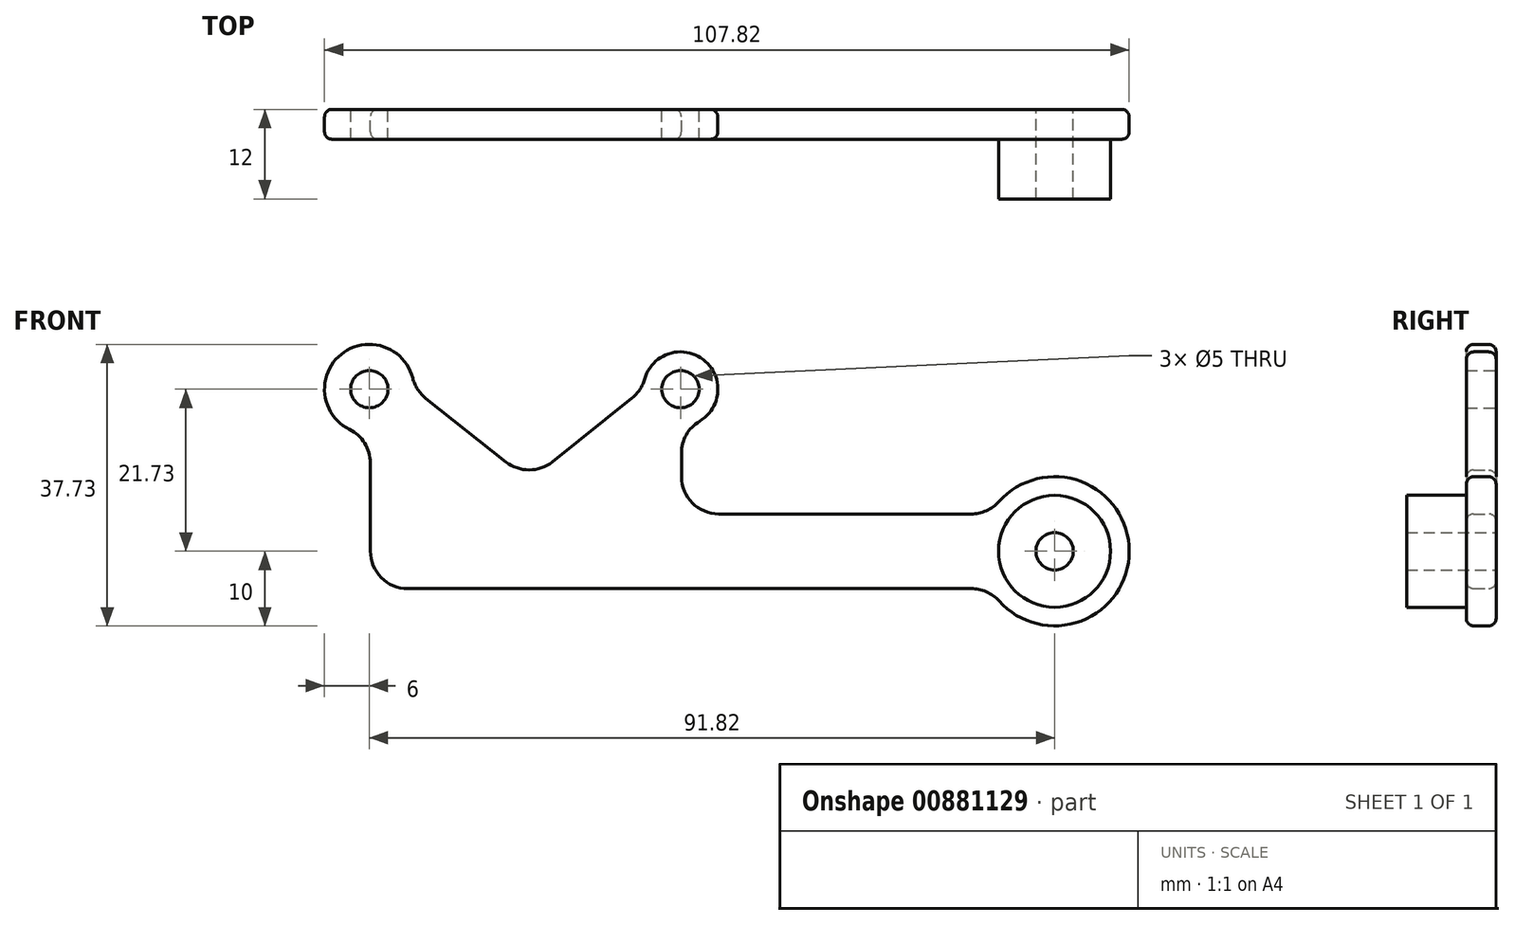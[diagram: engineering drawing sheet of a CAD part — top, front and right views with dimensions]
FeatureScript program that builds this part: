
annotation { "Feature Type Name" : "Feature", "Feature Type Description" : "" }
export const myFeature = defineFeature(function(context is Context, id is Id, definition is map)
    precondition{}
    {
        {
            var Q0;
            Q0=qCreatedBy(makeId("Front.planeOp"),FACE);
            var sketch = newSketch(context, id + "F0", { "sketchPlane" : qUnion([Q0])});
            skCircle(sketch, "E0", {"center": v(0, 0) * mm, "radius": 2.5 * mm});
            skCircle(sketch, "E1", {"center": v(41.7, 0) * mm, "radius": 2.5 * mm});
            skArc(sketch, "E2", {"start": v(5.82, 1.46) * mm, "mid": v(-3.77, 4.67) * mm, "end": v(-2.65, -5.38) * mm});
            skArc(sketch, "E3", {"start": v(44.26, -4.3) * mm, "mid": v(44.74, 3.97) * mm, "end": v(36.89, 1.35) * mm});
            skLineSegment(sketch, "E4", {"start": v(0.14, -9.87) * mm, "end": v(0.14, -21.73) * mm});
            skPoint(sketch, "E5.visualSharp", {"position": v(0.14, -6) * mm});
            skArc(sketch, "E5.filletArc", {"start": v(0.14, -9.87) * mm, "mid": v(-0.61, -7.23) * mm, "end": v(-2.65, -5.38) * mm});
            skPoint(sketch, "E6.visualSharp", {"position": v(41.82, -5) * mm});
            skArc(sketch, "E6.filletArc", {"start": v(44.26, -4.3) * mm, "mid": v(42.47, -6.12) * mm, "end": v(41.82, -8.59) * mm});
            skPoint(sketch, "E7.visualSharp", {"position": v(6, 0) * mm});
            skPoint(sketch, "E8.visualSharp", {"position": v(36.7, 0) * mm});
            skCircle(sketch, "E9", {"center": v(91.82, -21.73) * mm, "radius": 2.5 * mm});
            skArc(sketch, "E10", {"start": v(84.37, -28.4) * mm, "mid": v(101.82, -21.73) * mm, "end": v(84.37, -15.06) * mm});
            skLineSegment(sketch, "E11.0", {"start": v(5.14, -26.73) * mm, "end": v(80.64, -26.73) * mm});
            skLineSegment(sketch, "E12.0", {"start": v(46.82, -16.73) * mm, "end": v(80.64, -16.73) * mm});
            skLineSegment(sketch, "E13.trimOffspring", {"start": v(41.82, -11.73) * mm, "end": v(41.82, -8.59) * mm});
            skPoint(sketch, "E14.visualSharp", {"position": v(41.82, -16.73) * mm});
            skArc(sketch, "E14.filletArc", {"start": v(41.82, -11.73) * mm, "mid": v(43.28, -15.27) * mm, "end": v(46.82, -16.73) * mm});
            skPoint(sketch, "E15.visualSharp", {"position": v(83.16, -16.73) * mm});
            skArc(sketch, "E15.filletArc", {"start": v(80.64, -16.73) * mm, "mid": v(82.68, -16.3) * mm, "end": v(84.37, -15.06) * mm});
            skPoint(sketch, "E16.visualSharp", {"position": v(83.16, -26.73) * mm});
            skArc(sketch, "E16.filletArc", {"start": v(84.37, -28.4) * mm, "mid": v(82.68, -27.17) * mm, "end": v(80.64, -26.73) * mm});
            skPoint(sketch, "E17.visualSharp", {"position": v(0.14, -26.73) * mm});
            skArc(sketch, "E17.filletArc", {"start": v(0.14, -21.73) * mm, "mid": v(1.6, -25.27) * mm, "end": v(5.14, -26.73) * mm});
            skLineSegment(sketch, "E18", {"start": v(7.56, -1.24) * mm, "end": v(18.3, -9.75) * mm});
            skLineSegment(sketch, "E19", {"start": v(24.53, -9.73) * mm, "end": v(35.2, -1.2) * mm});
            skArc(sketch, "E20.filletArc", {"start": v(5.82, 1.46) * mm, "mid": v(6.47, -0.03) * mm, "end": v(7.56, -1.24) * mm});
            skArc(sketch, "E21.filletArc", {"start": v(35.2, -1.2) * mm, "mid": v(36.24, -0.06) * mm, "end": v(36.89, 1.35) * mm});
            skPoint(sketch, "E22.visualSharp", {"position": v(21.42, -12.22) * mm});
            skArc(sketch, "E22.filletArc", {"start": v(18.3, -9.75) * mm, "mid": v(21.42, -10.83) * mm, "end": v(24.53, -9.73) * mm});
            skSolve(sketch);
        }
        {
            var Q0;
            Q0=makeQuery(id+"F0.imprint","IMPRINT",FACE,{"disambiguationData":[TD([[makeQuery(id+"F0.imprint","IMPRINT",EDGE,{"derivedFrom":sQuery(id+"F0.wireOp",EDGE,"E0")}),-1.0]])]});
            extrude(context, id + "F1", {"entities" : qUnion([Q0]), "depth" : 4 * mm, "offsetDistance" : 25 * mm});
        }
        {
            var Q0;
            Q0=makeQuery(id+"F1.opExtrude","CAP_FACE",FACE,{"disambiguationData":[OSD([sQuery(id+"F0.wireOp",EDGE,"E0"),sQuery(id+"F0.wireOp",EDGE,"E1"),sQuery(id+"F0.wireOp",EDGE,"E2"),sQuery(id+"F0.wireOp",EDGE,"E3"),sQuery(id+"F0.wireOp",EDGE,"E4"),sQuery(id+"F0.wireOp",EDGE,"i2JHUBwB-WoMS-hNja-B1AR-gZhFcR5SSLUY"),sQuery(id+"F0.wireOp",EDGE,"gAJx2Sjt-7kl2-5VKp-IZuG-jDea5eaO6RQb"),sQuery(id+"F0.wireOp",EDGE,"E5.filletArc"),sQuery(id+"F0.wireOp",EDGE,"E6.filletArc"),sQuery(id+"F0.wireOp",EDGE,"ynXhVWPZ-49Mz-JrMB-5Ug1-2tgY13rhSzcD"),sQuery(id+"F0.wireOp",EDGE,"E7.filletArc"),sQuery(id+"F0.wireOp",EDGE,"E8.filletArc"),sQuery(id+"F0.wireOp",EDGE,"f5rfgzuo-szDQ-Me6B-WNCq-ZlnOoBMhrVJD"),sQuery(id+"F0.wireOp",EDGE,"E9"),sQuery(id+"F0.wireOp",EDGE,"E10"),sQuery(id+"F0.wireOp",EDGE,"E11.0"),sQuery(id+"F0.wireOp",EDGE,"E12.0"),sQuery(id+"F0.wireOp",EDGE,"E13.trimOffspring"),sQuery(id+"F0.wireOp",EDGE,"E14.filletArc"),sQuery(id+"F0.wireOp",EDGE,"3a682c63-b88b-40e8-9996-1dfc8cae14ac.filletArc"),sQuery(id+"F0.wireOp",EDGE,"E15.filletArc"),sQuery(id+"F0.wireOp",EDGE,"E16.filletArc")])],"isStart":false});
            var sketch = newSketch(context, id + "F2", { "sketchPlane" : qUnion([Q0])});
            skCircle(sketch, "E23", {"center": v(91.82, -21.73) * mm, "radius": 7.5 * mm});
            skCircle(sketch, "E24", {"center": v(91.82, -21.73) * mm, "radius": 2.5 * mm});
            skSolve(sketch);
        }
        {
            var Q0;
            Q0=makeQuery(id+"F2.imprint","IMPRINT",FACE,{"disambiguationData":[TD([[makeQuery(id+"F2.imprint","IMPRINT",EDGE,{"derivedFrom":sQuery(id+"F2.wireOp",EDGE,"E23")}),1.0]])]});
            extrude(context, id + "F3", {"entities" : qUnion([Q0]), "operationType" : NewBodyOperationType.ADD, "depth" : 8 * mm, "offsetDistance" : 25 * mm});
        }
        {
            var Q0;
            Q0=makeQuery(id+"F1.opExtrude","CAP_EDGE",EDGE,{"disambiguationData":[OSD([sQuery(id+"F0.wireOp",EDGE,"E18")])],"isStart":false});
            var Q1;
            Q1=makeQuery(id+"F1.opExtrude","CAP_EDGE",EDGE,{"disambiguationData":[OSD([sQuery(id+"F0.wireOp",EDGE,"E12.0")])],"isStart":true});
            fillet(context, id + "F4", {"entities" : qUnion([Q0, Q1]), "radius" : 1 * mm, "tangentPropagation" : true, "allowEdgeOverflow" : false});
        }
    });
